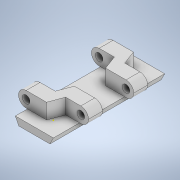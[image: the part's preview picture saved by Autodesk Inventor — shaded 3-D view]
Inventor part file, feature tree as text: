
AUTODESK INVENTOR PART (.ipt)
format: ipt  version: 2022 (Build 260153000, 153)  size: 244,224 bytes
history: native  units: mm
features: sketch x6, extrude x5, fillet x1
ambient origin geometry x8: Origin, YZ Plane, XZ Plane, XY Plane, X Axis, Y Axis, Z Axis, Center Point
bodies: Solid1 (feature_tree)
feature tree (12):
  extrude  "Extrusion1"  Depth=10.9556mm
  extrude  "Extrusion2"  Depth=1.0mm
  extrude  "Extrusion3"  TaperAngle=0.0deg  [1 undecoded]
  fillet  "Fillet1"  Radius=32.0mm
  extrude  "Extrusion4"  Depth=2.0mm
  extrude  "Extrusion5"  Depth=8.0mm
  sketch  "Sketch6"  dims[d14=0.5384mm d15=2.0524mm d16=1.5mm d17=1.5mm d23=0.538mm d24=2.052mm d25=1.5mm d26=1.5mm d27=0.538mm d28=2.052mm d29=0.538mm d30=4.4114mm d31=0.0mm d32=2.2055mm d33=1.5mm d34=1.5mm d35=4.4114mm d36=0.0mm d37=1.5mm d38=1.5mm d39=2.2mm d40=2.2mm d41=0.0mm d42=0.0mm d43=1.5mm d44=1.5mm]
  sketch  "Sketch1"  dims[d0=32.0mm d1=10.9556mm]
  sketch  "Sketch2"  dims[d2=2.0mm d3=0.0mm d4=1.0mm]
  sketch  "Sketch3"  dims[d5=1.0mm d6=0.0mm d7=0.0mm d8=32.0mm]
  sketch  "Sketch4"  dims[d10=2.0mm d11=2.0mm]
  sketch  "Sketch5"  dims[d12=8.0mm d13=8.0mm]
note: 1 required parameter value undecoded (feature->parameter linkage not recoverable at this tier; creation-order binding heuristic only, values carry confidence <= 0.55)
